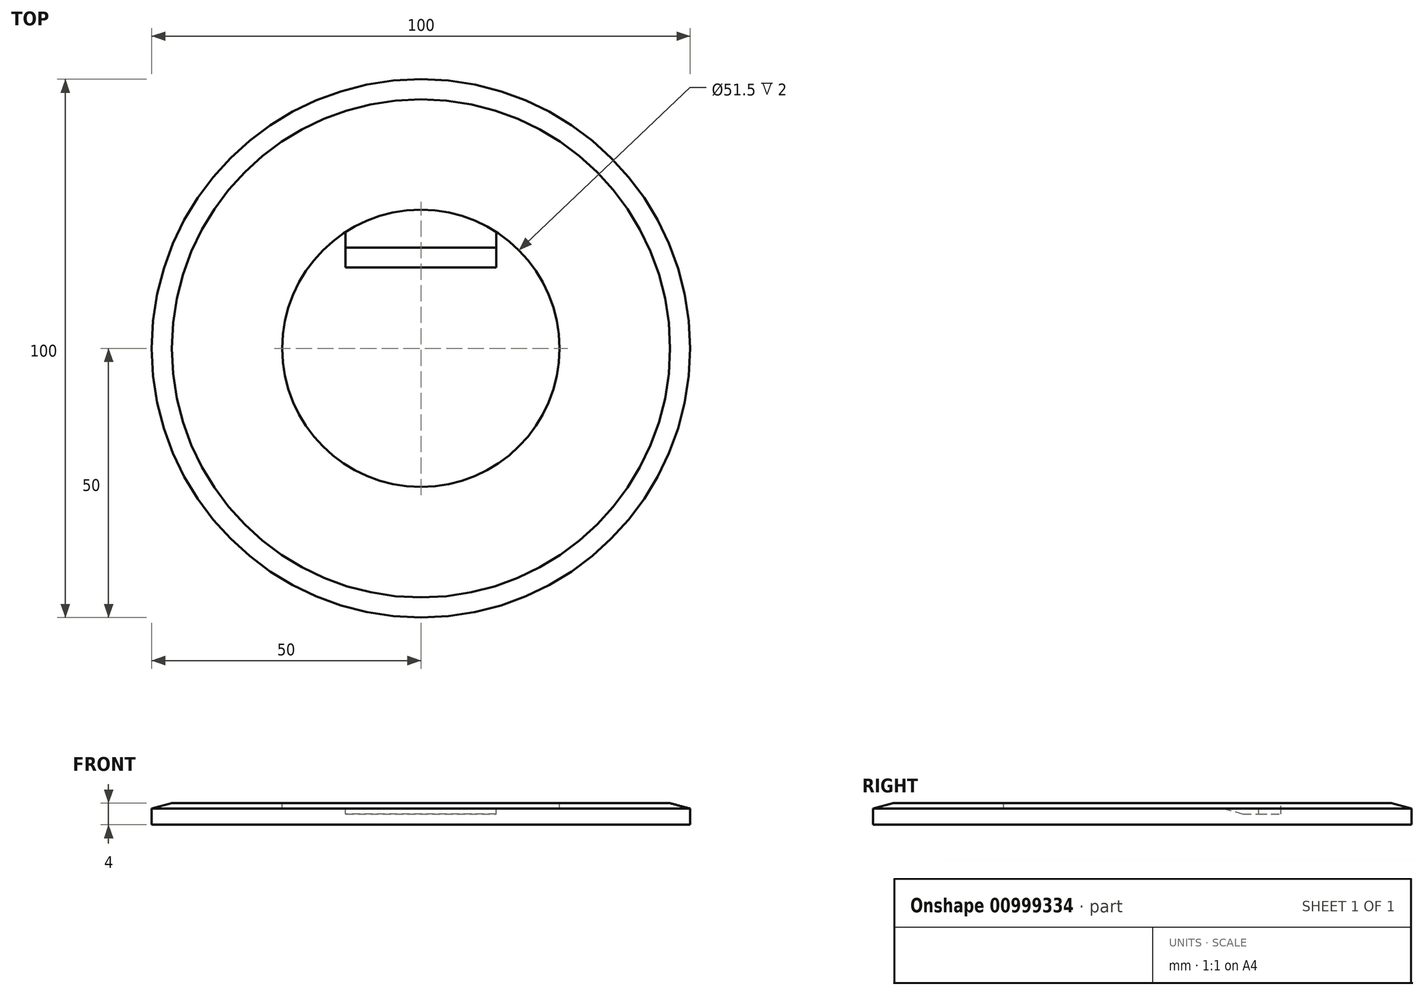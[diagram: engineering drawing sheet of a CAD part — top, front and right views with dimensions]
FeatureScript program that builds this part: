
annotation { "Feature Type Name" : "Feature", "Feature Type Description" : "" }
export const myFeature = defineFeature(function(context is Context, id is Id, definition is map)
    precondition{}
    {
        {
            var Q0;
            Q0=qCreatedBy(makeId("Top.planeOp"),FACE);
            var sketch = newSketch(context, id + "F0", { "sketchPlane" : qUnion([Q0])});
            skCircle(sketch, "E0", {"center": v(0, 0) * mm, "radius": 50 * mm});
            skSolve(sketch);
        }
        {
            var Q0;
            Q0=makeQuery(id+"F0.imprint","IMPRINT",FACE,{"disambiguationData":[TD([[makeQuery(id+"F0.imprint","IMPRINT",EDGE,{"derivedFrom":sQuery(id+"F0.wireOp",EDGE,"E0")}),1.0]])]});
            extrude(context, id + "F1", {"entities" : qUnion([Q0]), "depth" : 4 * mm, "offsetDistance" : 25 * mm});
        }
        {
            var Q0;
            Q0=makeQuery(id+"F1.opExtrude","CAP_FACE",FACE,{"disambiguationData":[OSD([sQuery(id+"F0.wireOp",EDGE,"E0")])],"isStart":false});
            var sketch = newSketch(context, id + "F2", { "sketchPlane" : qUnion([Q0])});
            skCircle(sketch, "E1", {"center": v(0, 0) * mm, "radius": 25.75 * mm});
            skSolve(sketch);
        }
        {
            var Q0;
            Q0=makeQuery(id+"F2.imprint","IMPRINT",FACE,{"disambiguationData":[TD([[makeQuery(id+"F2.imprint","IMPRINT",EDGE,{"derivedFrom":sQuery(id+"F2.wireOp",EDGE,"E1")}),1.0]])]});
            extrude(context, id + "F3", {"entities" : qUnion([Q0]), "operationType" : NewBodyOperationType.REMOVE, "oppositeDirection" : true, "depth" : 1 * mm, "offsetDistance" : 25 * mm});
        }
        {
            var Q0;
            Q0=makeQuery(id+"F1.opExtrude","CAP_FACE",FACE,{"disambiguationData":[OSD([sQuery(id+"F0.wireOp",EDGE,"E0")])],"isStart":false});
            var sketch = newSketch(context, id + "F4", { "sketchPlane" : qUnion([Q0])});
            skLineSegment(sketch, "E2.bottom", {"start": v(-14, 15) * mm, "end": v(14, 15) * mm});
            skLineSegment(sketch, "E2.top", {"start": v(-14, 55) * mm, "end": v(14, 55) * mm});
            skLineSegment(sketch, "E2.left", {"start": v(-14, 15) * mm, "end": v(-14, 55) * mm});
            skLineSegment(sketch, "E2.right", {"start": v(14, 15) * mm, "end": v(14, 55) * mm});
            skSolve(sketch);
        }
        {
            var Q0;
            {var subQ0=sQuery(id+"F4.wireOp",EDGE,"E2.left");var subQ1=sQuery(id+"F4.wireOp",EDGE,"E2.bottom");var subQ2=makeQuery(id+"F3.boolean.opBoolean","COPY",EDGE,{"derivedFrom":makeQuery(id+"F3.opExtrude","CAP_EDGE",EDGE,{"disambiguationData":[OSD([sQuery(id+"F2.wireOp",EDGE,"E1")])],"isStart":true})});var subQ3=makeQuery(id+"F4.imprint","INTERSECT",VERTEX,{"derivedFrom":[subQ2,subQ1,subQ0]});Q0=makeQuery(id+"F4.imprint","IMPRINT",FACE,{"disambiguationData":[TD([[makeQuery(id+"F4.imprint","IMPRINT",EDGE,{"disambiguationData":[TD([[subQ3,-1.0]])],"derivedFrom":subQ0}),-1.0]])]});}
            var Q1;
            {var subQ3=sQuery(id+"F4.wireOp",EDGE,"Pzhda29Q-4lAh-gGU2-DwRu-Ev0d9NLUe20T.bottom");Q1=makeQuery(id+"F4.imprint","IMPRINT",FACE,{"disambiguationData":[TD([[makeQuery(id+"F4.imprint","IMPRINT",EDGE,{"derivedFrom":subQ3}),1.0]])]});}
            var Q2;
            Q2=makeQuery(id+"F4.imprint","IMPRINT",FACE,{"disambiguationData":[TD([[makeQuery(id+"F4.imprint","IMPRINT",EDGE,{"derivedFrom":sQuery(id+"F4.wireOp",EDGE,"Pzhda29Q-4lAh-gGU2-DwRu-Ev0d9NLUe20T.bottom")}),-1.0]])]});
            var Q3;
            {var subQ0=sQuery(id+"F4.wireOp",EDGE,"E2.top");Q3=makeQuery(id+"F4.imprint","IMPRINT",FACE,{"disambiguationData":[TD([[makeQuery(id+"F4.imprint","IMPRINT",EDGE,{"derivedFrom":subQ0}),-1.0]])]});}
            extrude(context, id + "F5", {"entities" : qUnion([Q0, Q1, Q2, Q3]), "operationType" : NewBodyOperationType.REMOVE, "oppositeDirection" : true, "depth" : 2 * mm, "offsetDistance" : 25 * mm});
        }
        {
            var Q0;
            Q0=makeQuery(id+"F5.boolean.opBoolean","COPY",EDGE,{"derivedFrom":makeQuery(id+"F5.opExtrude","CAP_EDGE",EDGE,{"disambiguationData":[OSD([sQuery(id+"F4.wireOp",EDGE,"E2.bottom")])],"isStart":false})});
            var Q1;
            Q1=makeQuery(id+"F1.opExtrude","CAP_EDGE",EDGE,{"disambiguationData":[OSD([sQuery(id+"F0.wireOp",EDGE,"E0")])],"isStart":false});
            var Q2;
            Q2=makeQuery(id+"F5.boolean.opBoolean","INTERSECT",EDGE,{"derivedFrom":[makeQuery(id+"F1.opExtrude","SWEPT_FACE",FACE,{"disambiguationData":[OSD([sQuery(id+"F0.wireOp",EDGE,"E0")])]}),makeQuery(id+"F5.opExtrude","CAP_FACE",FACE,{"disambiguationData":[OSD([sQuery(id+"F4.wireOp",EDGE,"E2.bottom"),sQuery(id+"F4.wireOp",EDGE,"E2.top"),sQuery(id+"F4.wireOp",EDGE,"E2.left"),sQuery(id+"F4.wireOp",EDGE,"E2.right")])],"isStart":false})]});
            chamfer(context, id + "F6", {"entities" : qUnion([Q0, Q1, Q2]), "chamferType" : ChamferType.OFFSET_ANGLE, "width" : 1 * mm, "oppositeDirection" : true, "angle" : 75 * degree, "tangentPropagation" : true});
        }
    });
